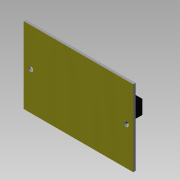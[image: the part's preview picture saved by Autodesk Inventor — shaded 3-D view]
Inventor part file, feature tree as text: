
AUTODESK INVENTOR PART (.ipt)
format: ipt  version: 2015 SP1 (Build 190203100, 203)  size: 109,568 bytes
history: native  units: mm
features: sketch x2, extrude x2
ambient origin geometry x8: Origin, YZ Plane, XZ Plane, XY Plane, X Axis, Y Axis, Z Axis, Center Point
bodies: Solid1 (feature_tree)
feature tree (4):
  sketch  "Sketch1"  dims[d0=78.56mm d1=54.61mm]
  extrude  "Extrusion1"  Depth=54.61mm
  extrude  "Extrusion2"  Depth=68.56mm
  sketch  "Sketch2"  dims[d2=3.5mm d3=5.0mm d4=3.5mm d5=5.0mm d6=27.0mm d7=10.0mm d8=5.0mm d9=27.0mm d10=10.0mm d11=5.0mm d12=1.7mm d13=0.0mm d14=16.58mm d15=0.0mm d16=68.56mm]
